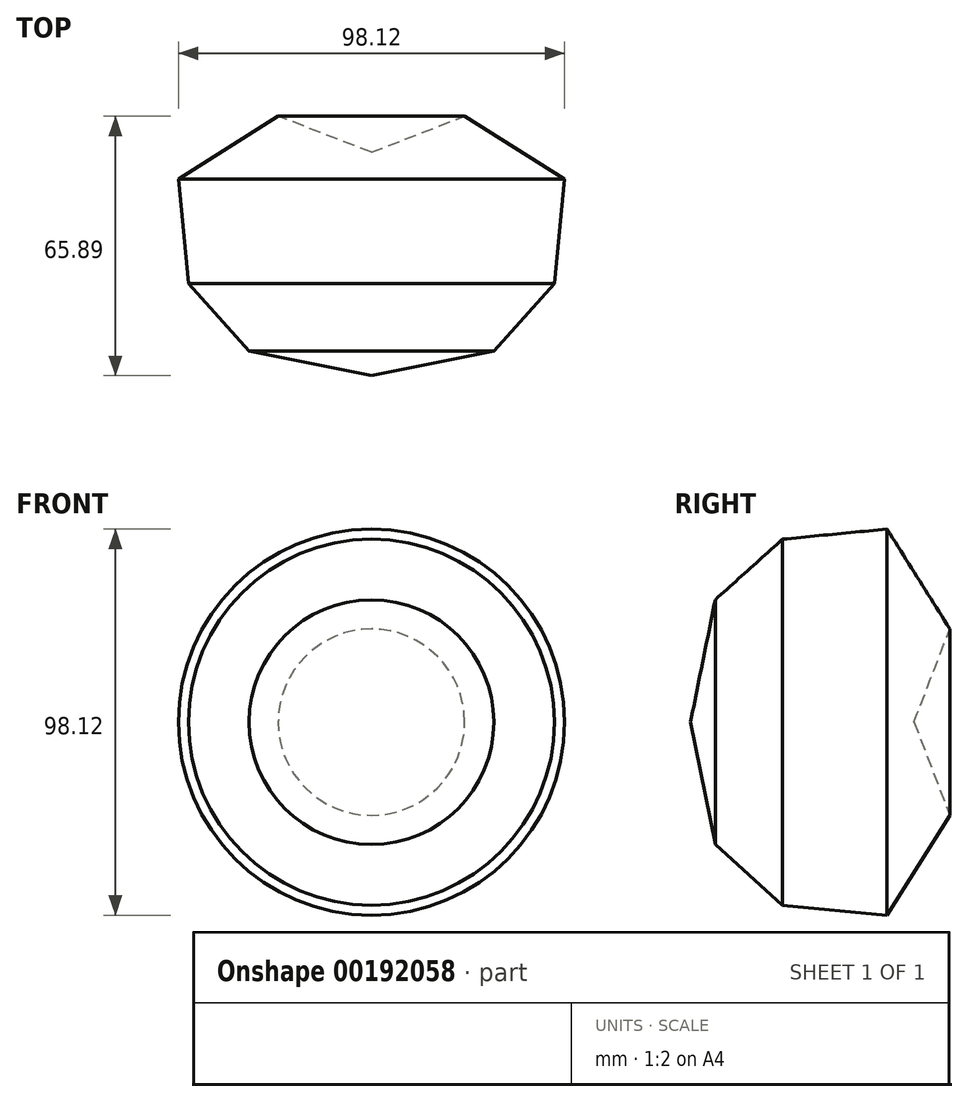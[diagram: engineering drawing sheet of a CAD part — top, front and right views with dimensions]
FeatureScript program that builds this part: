
annotation { "Feature Type Name" : "Feature", "Feature Type Description" : "" }
export const myFeature = defineFeature(function(context is Context, id is Id, definition is map)
    precondition{}
    {
        {
            var Q0;
            Q0=qCreatedBy(makeId("Top.planeOp"),FACE);
            var sketch = newSketch(context, id + "F0", { "sketchPlane" : qUnion([Q0])});
            skLineSegment(sketch, "E0", {"start": v(0, 36.65) * mm, "end": v(0, -20.1) * mm});
            skLineSegment(sketch, "E1", {"start": v(0, -20.1) * mm, "end": v(31.1, -13.83) * mm});
            skLineSegment(sketch, "E2", {"start": v(31.1, -13.83) * mm, "end": v(46.5, 3.28) * mm});
            skLineSegment(sketch, "E3", {"start": v(46.5, 3.28) * mm, "end": v(49.06, 29.8) * mm});
            skLineSegment(sketch, "E4", {"start": v(49.06, 29.8) * mm, "end": v(23.67, 45.78) * mm});
            skLineSegment(sketch, "E5", {"start": v(23.67, 45.78) * mm, "end": v(0, 36.65) * mm});
            skSolve(sketch);
        }
        {
            var Q0;
            Q0 = qSketchRegion(id + "F0", true);
            var Q1;
            Q1=sQuery(id+"F0.wireOp",EDGE,"E0");
            revolve(context, id + "F1", {"entities" : qUnion([Q0]), "axis" : qUnion([Q1]), "revolveType" : RevolveType.FULL});
        }
    });
